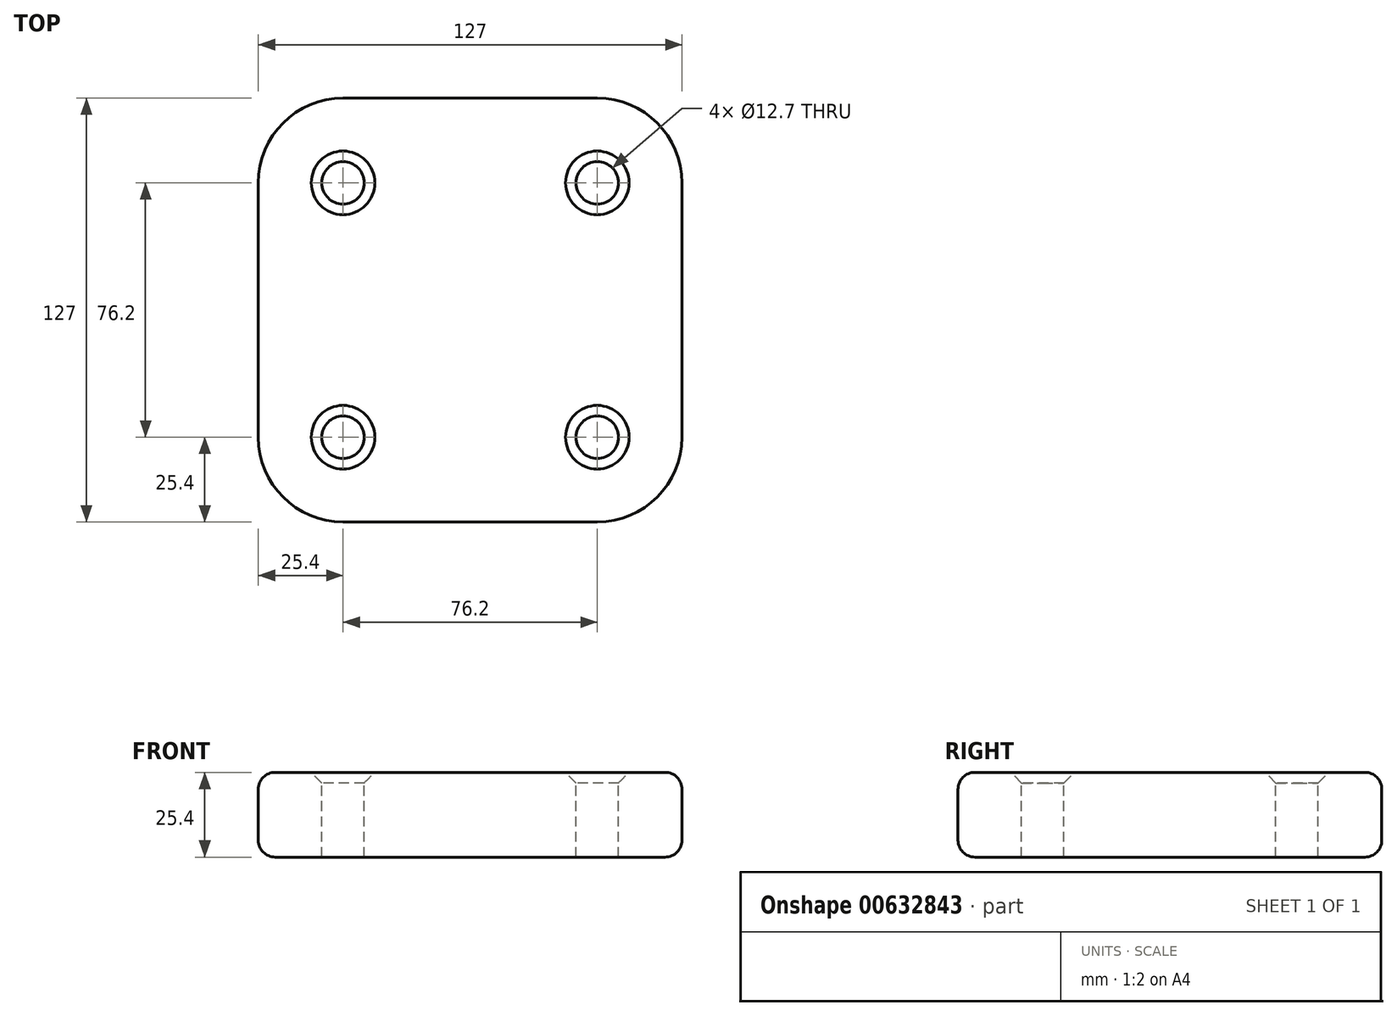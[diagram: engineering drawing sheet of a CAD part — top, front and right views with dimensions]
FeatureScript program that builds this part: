
annotation { "Feature Type Name" : "Feature", "Feature Type Description" : "" }
export const myFeature = defineFeature(function(context is Context, id is Id, definition is map)
    precondition{}
    {
        {
            var Q0;
            Q0=qCreatedBy(makeId("Top.planeOp"),FACE);
            var sketch = newSketch(context, id + "F0", { "sketchPlane" : qUnion([Q0])});
            skLineSegment(sketch, "E0.bottom", {"start": v(-63.5, 63.5) * mm, "end": v(63.5, 63.5) * mm});
            skLineSegment(sketch, "E0.top", {"start": v(-63.5, -63.5) * mm, "end": v(63.5, -63.5) * mm});
            skLineSegment(sketch, "E0.left", {"start": v(-63.5, 63.5) * mm, "end": v(-63.5, -63.5) * mm});
            skLineSegment(sketch, "E0.right", {"start": v(63.5, 63.5) * mm, "end": v(63.5, -63.5) * mm});
            skSolve(sketch);
        }
        {
            var Q0;
            Q0 = qSketchRegion(id + "F0", true);
            extrude(context, id + "F1", {"entities" : qUnion([Q0]), "depth" : 25.4 * mm, "offsetDistance" : 25.4 * mm});
        }
        {
            var Q0;
            Q0=makeQuery(id+"F1.opExtrude","SWEPT_EDGE",EDGE,{"disambiguationData":[OSD([sQuery(id+"F0.wireOp",EDGE,"E0.top"),sQuery(id+"F0.wireOp",EDGE,"E0.right")])]});
            var Q1;
            Q1=makeQuery(id+"F1.opExtrude","SWEPT_EDGE",EDGE,{"disambiguationData":[OSD([sQuery(id+"F0.wireOp",EDGE,"E0.bottom"),sQuery(id+"F0.wireOp",EDGE,"E0.right")])]});
            var Q2;
            Q2=makeQuery(id+"F1.opExtrude","SWEPT_EDGE",EDGE,{"disambiguationData":[OSD([sQuery(id+"F0.wireOp",EDGE,"E0.top"),sQuery(id+"F0.wireOp",EDGE,"E0.left")])]});
            var Q3;
            Q3=makeQuery(id+"F1.opExtrude","SWEPT_EDGE",EDGE,{"disambiguationData":[OSD([sQuery(id+"F0.wireOp",EDGE,"E0.bottom"),sQuery(id+"F0.wireOp",EDGE,"E0.left")])]});
            fillet(context, id + "F2", {"entities" : qUnion([Q0, Q1, Q2, Q3]), "radius" : 25.4 * mm, "tangentPropagation" : true, "allowEdgeOverflow" : false});
        }
        {
            var Q0;
            Q0=makeQuery(id+"F1.opExtrude","CAP_EDGE",EDGE,{"disambiguationData":[OSD([sQuery(id+"F0.wireOp",EDGE,"E0.top")])],"isStart":false});
            var Q1;
            Q1=makeQuery(id+"F1.opExtrude","CAP_EDGE",EDGE,{"disambiguationData":[OSD([sQuery(id+"F0.wireOp",EDGE,"E0.top")])],"isStart":true});
            fillet(context, id + "F3", {"entities" : qUnion([Q0, Q1]), "radius" : 5.08 * mm, "tangentPropagation" : true, "allowEdgeOverflow" : false});
        }
        {
            var Q0;
            Q0=makeQuery(id+"F1.opExtrude","CAP_FACE",FACE,{"disambiguationData":[OSD([sQuery(id+"F0.wireOp",EDGE,"E0.bottom"),sQuery(id+"F0.wireOp",EDGE,"E0.top"),sQuery(id+"F0.wireOp",EDGE,"E0.left"),sQuery(id+"F0.wireOp",EDGE,"E0.right")])],"isStart":false});
            var sketch = newSketch(context, id + "F4", { "sketchPlane" : qUnion([Q0])});
            skCircle(sketch, "E1", {"center": v(-38.1, 38.1) * mm, "radius": 6.35 * mm});
            skCircle(sketch, "E2.MirrorC", {"center": v(38.1, 38.1) * mm, "radius": 6.35 * mm});
            skCircle(sketch, "E3.MirrorC", {"center": v(-38.1, -38.1) * mm, "radius": 6.35 * mm});
            skCircle(sketch, "E4.MirrorC", {"center": v(38.1, -38.1) * mm, "radius": 6.35 * mm});
            skSolve(sketch);
        }
        {
            var Q0;
            Q0=sQuery(id+"F4.wireOp",VERTEX,"E3.MirrorC.center");
            var Q1;
            Q1=sQuery(id+"F4.wireOp",VERTEX,"E1.center");
            var Q2;
            Q2=sQuery(id+"F4.wireOp",VERTEX,"E4.MirrorC.center");
            var Q3;
            Q3=sQuery(id+"F4.wireOp",VERTEX,"E2.MirrorC.center");
            var Q4;
            Q4=makeQuery(id+"F1.opExtrude","SWEPT_BODY",BODY,{"disambiguationData":[OSD([sQuery(id+"F0.wireOp",EDGE,"E0.bottom"),sQuery(id+"F0.wireOp",EDGE,"E0.top"),sQuery(id+"F0.wireOp",EDGE,"E0.left"),sQuery(id+"F0.wireOp",EDGE,"E0.right")])]});
            hole(context, id + "F5", {"style" : HoleStyle.C_SINK, "endStyle" : HoleEndStyle.THROUGH, "holeDiameter" : 12.7 * mm, "cSinkDiameter" : 19.05 * mm, "cSinkAngle" : 90 * degree, "majorDiameter" : 6.35 * mm, "isTappedThrough" : true, "tappedDepth" : 12.7 * mm, "tapClearance" : 3, "locations" : qUnion([Q0, Q1, Q2, Q3]), "scope" : qUnion([Q4])});
        }
    });
